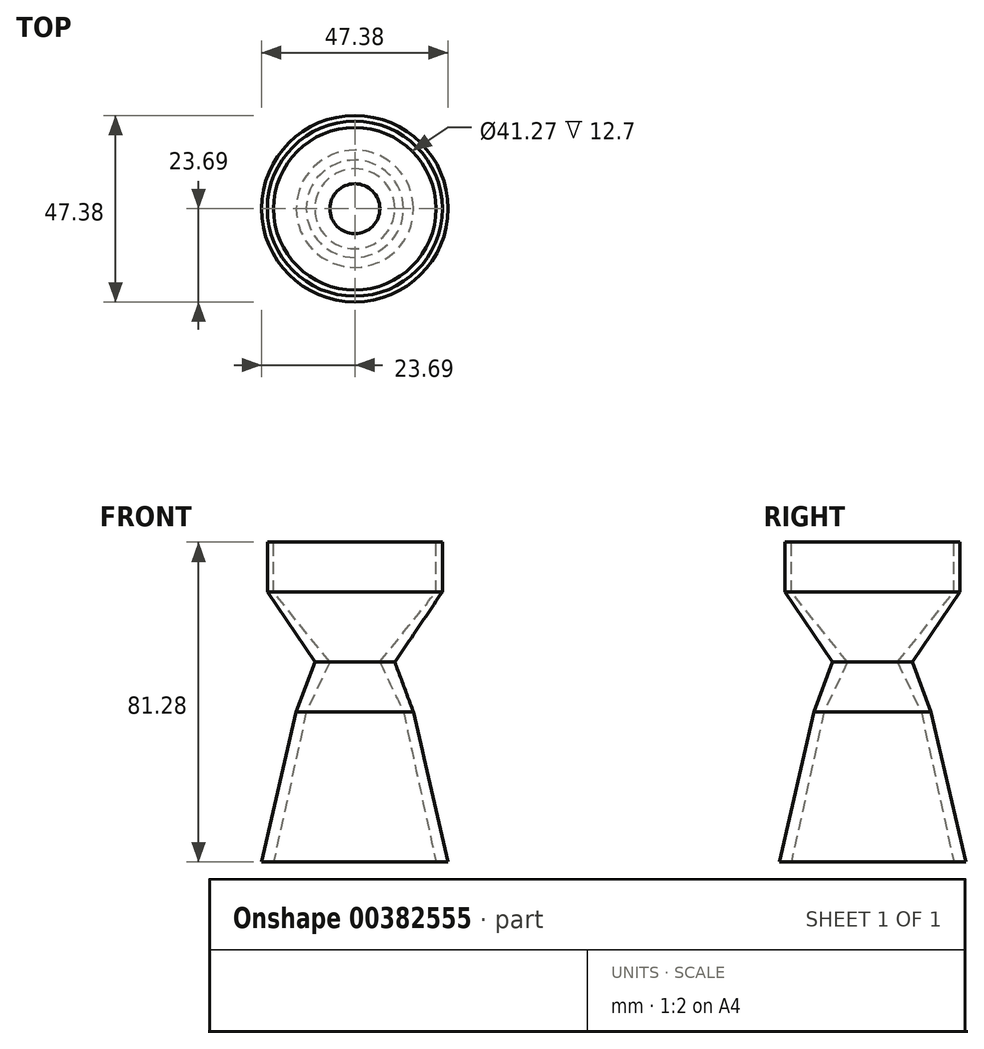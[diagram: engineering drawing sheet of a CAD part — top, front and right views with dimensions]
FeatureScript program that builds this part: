
annotation { "Feature Type Name" : "Feature", "Feature Type Description" : "" }
export const myFeature = defineFeature(function(context is Context, id is Id, definition is map)
    precondition{}
    {
        {
            var Q0;
            Q0=qCreatedBy(makeId("Top.planeOp"),FACE);
            var sketch = newSketch(context, id + "F0", { "sketchPlane" : qUnion([Q0])});
            skCircle(sketch, "E0", {"center": v(0, 0) * mm, "radius": 20.64 * mm});
            skSolve(sketch);
        }
        {
            var Q0;
            Q0=qCreatedBy(makeId("Top.planeOp"),FACE);
            var sketch = newSketch(context, id + "F1", { "sketchPlane" : qUnion([Q0])});
            skCircle(sketch, "E1", {"center": v(0, 0) * mm, "radius": 22.23 * mm});
            skSolve(sketch);
        }
        {
            var Q0;
            Q0=qCreatedBy(makeId("Top.planeOp"),FACE);
            cPlane(context, id + "F2", {"entities" : qUnion([Q0]), "cplaneType" : CPlaneType.OFFSET, "offset" : 12.7 * mm, "width" : 152.4 * mm, "height" : 152.4 * mm});
        }
        {
            var Q0;
            Q0=qCreatedBy(id+"F2.planeOp",FACE);
            var sketch = newSketch(context, id + "F3", { "sketchPlane" : qUnion([Q0])});
            skCircle(sketch, "E2", {"center": v(0, 0) * mm, "radius": 20.64 * mm});
            skSolve(sketch);
        }
        {
            var Q0;
            Q0=qCreatedBy(id+"F2.planeOp",FACE);
            var sketch = newSketch(context, id + "F4", { "sketchPlane" : qUnion([Q0])});
            skCircle(sketch, "E3", {"center": v(0, 0) * mm, "radius": 22.23 * mm});
            skSolve(sketch);
        }
        {
            var Q0;
            Q0 = qSketchRegion(id + "F1", true);
            var Q1;
            Q1 = qSketchRegion(id + "F4", true);
            loft(context, id + "F5", {"sheetProfilesArray" : [{ "sheetProfileEntities" : qUnion([Q0]) }, { "sheetProfileEntities" : qUnion([Q1]) }]});
        }
        {
            var Q1;
            Q1 = qSketchRegion(id + "F0", true);
            var Q2;
            Q2 = qSketchRegion(id + "F3", true);
            loft(context, id + "F6", {"operationType" : NewBodyOperationType.REMOVE, "sheetProfilesArray" : [{ "sheetProfileEntities" : qUnion([Q1]) }, { "sheetProfileEntities" : qUnion([Q2]) }]});
        }
        {
            var Q0;
            Q0=qCreatedBy(makeId("Top.planeOp"),FACE);
            cPlane(context, id + "F7", {"entities" : qUnion([Q0]), "cplaneType" : CPlaneType.OFFSET, "offset" : 17.78 * mm, "oppositeDirection" : true, "width" : 152.4 * mm, "height" : 152.4 * mm});
        }
        {
            var Q0;
            Q0=qCreatedBy(id+"F7.planeOp",FACE);
            var sketch = newSketch(context, id + "F8", { "sketchPlane" : qUnion([Q0])});
            skCircle(sketch, "E4", {"center": v(0, 0) * mm, "radius": 6.35 * mm});
            skSolve(sketch);
        }
        {
            var Q0;
            Q0=qCreatedBy(id+"F7.planeOp",FACE);
            var sketch = newSketch(context, id + "F9", { "sketchPlane" : qUnion([Q0])});
            skCircle(sketch, "E5", {"center": v(0, 0) * mm, "radius": 10.16 * mm});
            skSolve(sketch);
        }
        {
            var Q1;
            Q1 = qSketchRegion(id + "F1", true);
            var Q2;
            Q2 = qSketchRegion(id + "F9", true);
            loft(context, id + "F10", {"operationType" : NewBodyOperationType.ADD, "sheetProfilesArray" : [{ "sheetProfileEntities" : qUnion([Q1]) }, { "sheetProfileEntities" : qUnion([Q2]) }]});
        }
        {
            var Q1;
            Q1 = qSketchRegion(id + "F8", true);
            var Q2;
            Q2 = qSketchRegion(id + "F0", true);
            loft(context, id + "F11", {"operationType" : NewBodyOperationType.REMOVE, "sheetProfilesArray" : [{ "sheetProfileEntities" : qUnion([Q1]) }, { "sheetProfileEntities" : qUnion([Q2]) }]});
        }
        {
            var Q0;
            Q0=qCreatedBy(id+"F7.planeOp",FACE);
            cPlane(context, id + "F12", {"entities" : qUnion([Q0]), "cplaneType" : CPlaneType.OFFSET, "offset" : 50.8 * mm, "oppositeDirection" : true, "width" : 152.4 * mm, "height" : 152.4 * mm});
        }
        {
            var Q0;
            Q0=qCreatedBy(id+"F12.planeOp",FACE);
            var sketch = newSketch(context, id + "F13", { "sketchPlane" : qUnion([Q0])});
            skCircle(sketch, "E6", {"center": v(0, 0) * mm, "radius": 20.62 * mm});
            skSolve(sketch);
        }
        {
            var Q0;
            Q0=qCreatedBy(id+"F7.planeOp",FACE);
            cPlane(context, id + "F14", {"entities" : qUnion([Q0]), "cplaneType" : CPlaneType.OFFSET, "offset" : 12.7 * mm, "oppositeDirection" : true, "width" : 152.4 * mm, "height" : 152.4 * mm});
        }
        {
            var Q0;
            Q0=qCreatedBy(id+"F14.planeOp",FACE);
            var sketch = newSketch(context, id + "F15", { "sketchPlane" : qUnion([Q0])});
            skCircle(sketch, "E7", {"center": v(0, 0) * mm, "radius": 12.36 * mm});
            skSolve(sketch);
        }
        {
            var Q0;
            Q0=qCreatedBy(id+"F14.planeOp",FACE);
            var sketch = newSketch(context, id + "F16", { "sketchPlane" : qUnion([Q0])});
            skCircle(sketch, "E8", {"center": v(0, 0) * mm, "radius": 14.9 * mm});
            skSolve(sketch);
        }
        {
            var Q1;
            Q1 = qSketchRegion(id + "F16", true);
            var Q2;
            Q2 = qSketchRegion(id + "F9", true);
            loft(context, id + "F17", {"operationType" : NewBodyOperationType.ADD, "sheetProfilesArray" : [{ "sheetProfileEntities" : qUnion([Q1]) }, { "sheetProfileEntities" : qUnion([Q2]) }]});
        }
        {
            var Q1;
            Q1 = qSketchRegion(id + "F15", true);
            var Q2;
            Q2 = qSketchRegion(id + "F8", true);
            loft(context, id + "F18", {"operationType" : NewBodyOperationType.REMOVE, "sheetProfilesArray" : [{ "sheetProfileEntities" : qUnion([Q1]) }, { "sheetProfileEntities" : qUnion([Q2]) }]});
        }
        {
            var Q0;
            Q0=qCreatedBy(id+"F12.planeOp",FACE);
            var sketch = newSketch(context, id + "F19", { "sketchPlane" : qUnion([Q0])});
            skCircle(sketch, "E9", {"center": v(0, 0) * mm, "radius": 23.69 * mm});
            skSolve(sketch);
        }
        {
            var Q1;
            Q1 = qSketchRegion(id + "F19", true);
            var Q2;
            Q2 = qSketchRegion(id + "F16", true);
            loft(context, id + "F20", {"operationType" : NewBodyOperationType.ADD, "sheetProfilesArray" : [{ "sheetProfileEntities" : qUnion([Q1]) }, { "sheetProfileEntities" : qUnion([Q2]) }]});
        }
        {
            var Q1;
            Q1 = qSketchRegion(id + "F15", true);
            var Q2;
            Q2 = qSketchRegion(id + "F13", true);
            loft(context, id + "F21", {"operationType" : NewBodyOperationType.REMOVE, "sheetProfilesArray" : [{ "sheetProfileEntities" : qUnion([Q1]) }, { "sheetProfileEntities" : qUnion([Q2]) }]});
        }
    });
